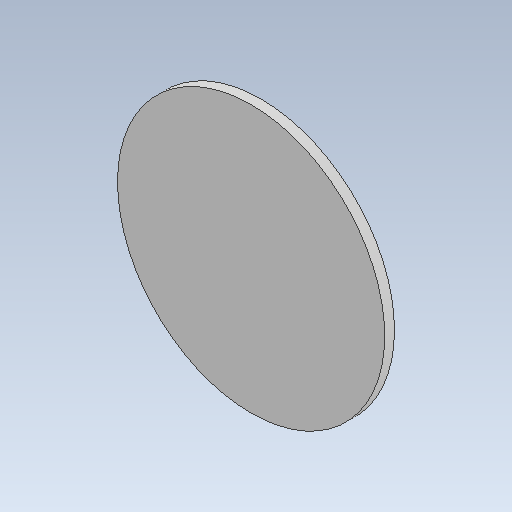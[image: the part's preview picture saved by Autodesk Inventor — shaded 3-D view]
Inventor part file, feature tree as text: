
AUTODESK INVENTOR PART (.ipt)
format: ipt  version: 2021 (Build 250183000, 183)  size: 93,184 bytes
history: native  units: mm
features: extrude x1, sketch x1
ambient origin geometry x8: Origin, YZ Plane, XZ Plane, XY Plane, X Axis, Y Axis, Z Axis, Center Point
bodies: Solide1 (feature_tree)
feature tree (2):
  extrude  "Extrusion1"  Depth=54.5mm
  sketch  "Esquisse1"
